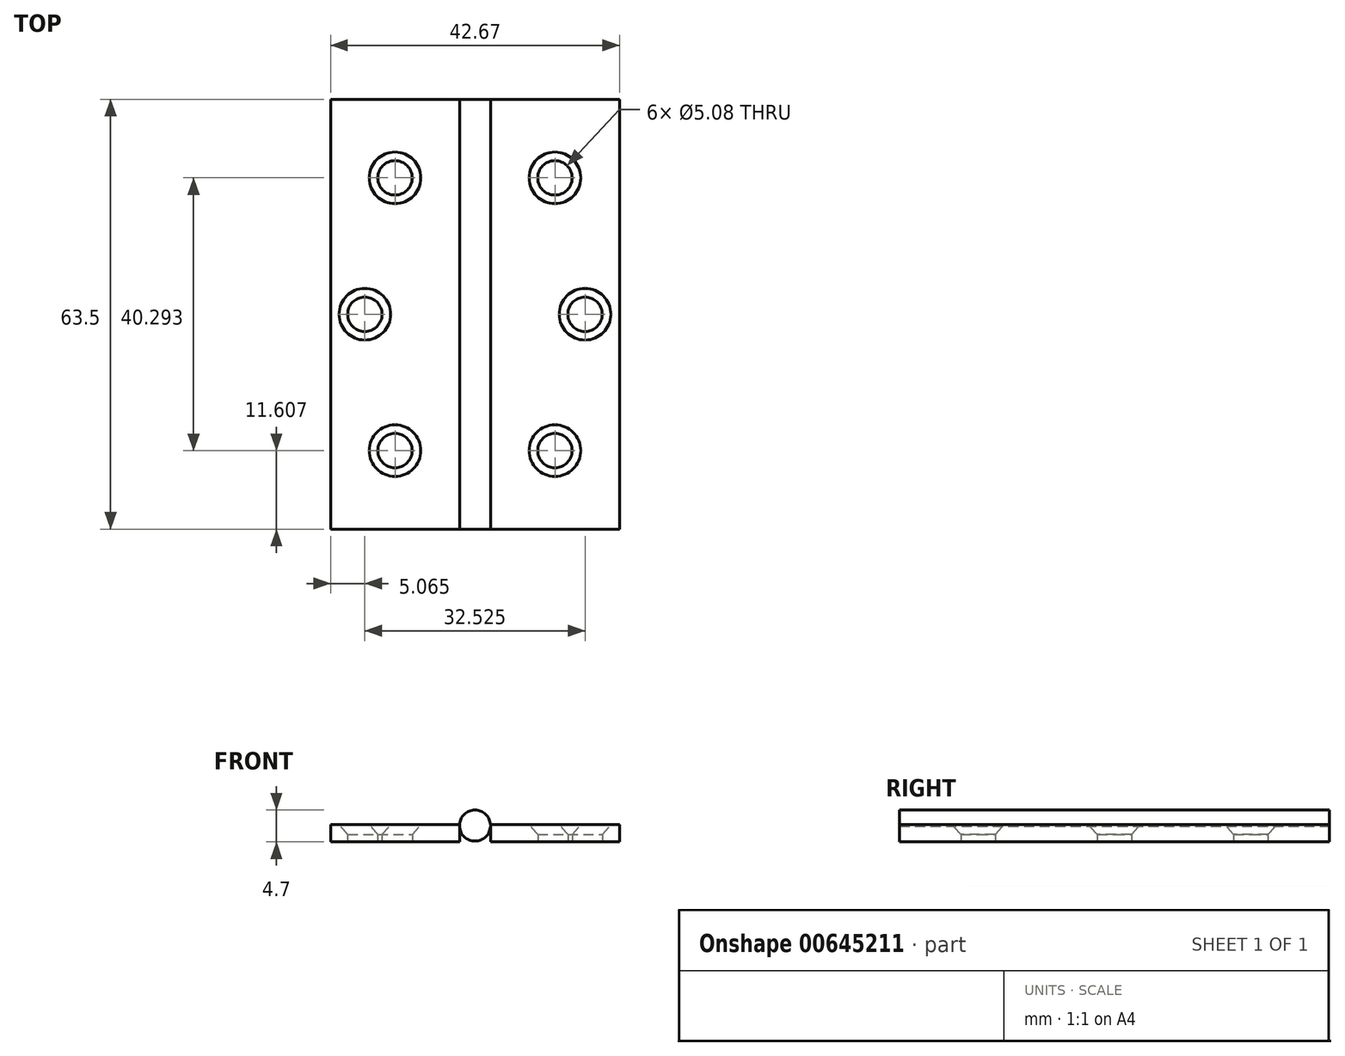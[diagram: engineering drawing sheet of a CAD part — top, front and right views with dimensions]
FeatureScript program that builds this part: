
annotation { "Feature Type Name" : "Feature", "Feature Type Description" : "" }
export const myFeature = defineFeature(function(context is Context, id is Id, definition is map)
    precondition{}
    {
        {
            var Q0;
            Q0=qCreatedBy(makeId("Top.planeOp"),FACE);
            var sketch = newSketch(context, id + "F0", { "sketchPlane" : qUnion([Q0])});
            skLineSegment(sketch, "E0.bottom", {"start": v(-55.16, 49.12) * mm, "end": v(-36.11, 49.12) * mm});
            skLineSegment(sketch, "E0.top", {"start": v(-55.16, -14.38) * mm, "end": v(-36.11, -14.38) * mm});
            skLineSegment(sketch, "E0.left", {"start": v(-55.16, 49.12) * mm, "end": v(-55.16, -14.38) * mm});
            skLineSegment(sketch, "E0.right", {"start": v(-36.11, 49.12) * mm, "end": v(-36.11, -14.38) * mm});
            skLineSegment(sketch, "E1.bottom", {"start": v(-31.54, -14.38) * mm, "end": v(-12.5, -14.38) * mm});
            skLineSegment(sketch, "E1.top", {"start": v(-31.54, 49.12) * mm, "end": v(-12.5, 49.12) * mm});
            skLineSegment(sketch, "E1.left", {"start": v(-31.54, -14.38) * mm, "end": v(-31.54, 49.12) * mm});
            skLineSegment(sketch, "E1.right", {"start": v(-12.5, -14.38) * mm, "end": v(-12.5, 49.12) * mm});
            skLineSegment(sketch, "E2", {"start": v(-45.64, 49.12) * mm, "end": v(-45.64, -14.38) * mm, "construction": true});
            skLineSegment(sketch, "E3", {"start": v(-22.02, -14.38) * mm, "end": v(-22.02, 49.12) * mm, "construction": true});
            skLineSegment(sketch, "E4", {"start": v(-12.5, 17.37) * mm, "end": v(-31.54, 17.37) * mm, "construction": true});
            skLineSegment(sketch, "E5", {"start": v(-36.11, 17.37) * mm, "end": v(-55.16, 17.37) * mm, "construction": true});
            skPoint(sketch, "E6", {"position": v(-22.02, -2.77) * mm});
            skPoint(sketch, "E7", {"position": v(-17.57, 17.37) * mm});
            skPoint(sketch, "E8", {"position": v(-22.02, 37.52) * mm});
            skPoint(sketch, "E9", {"position": v(-45.64, 37.52) * mm});
            skPoint(sketch, "E10", {"position": v(-50.1, 17.37) * mm});
            skPoint(sketch, "E11", {"position": v(-45.64, -2.77) * mm});
            skSolve(sketch);
        }
        {
            var Q0;
            Q0=makeQuery(id+"F0.imprint","IMPRINT",FACE,{"disambiguationData":[TD([[makeQuery(id+"F0.imprint","IMPRINT",EDGE,{"derivedFrom":sQuery(id+"F0.wireOp",EDGE,"E0.bottom")}),-1.0]])]});
            var Q1;
            Q1=makeQuery(id+"F0.imprint","IMPRINT",FACE,{"disambiguationData":[TD([[makeQuery(id+"F0.imprint","IMPRINT",EDGE,{"derivedFrom":sQuery(id+"F0.wireOp",EDGE,"E1.bottom")}),1.0]])]});
            extrude(context, id + "F1", {"entities" : qUnion([Q0, Q1]), "depth" : 2.54 * mm, "offsetDistance" : 25.4 * mm});
        }
        {
            var Q0;
            Q0=makeQuery(id+"F1.opExtrude","SWEPT_FACE",FACE,{"disambiguationData":[OSD([sQuery(id+"F0.wireOp",EDGE,"E0.bottom")])]});
            var sketch = newSketch(context, id + "F2", { "sketchPlane" : qUnion([Q0])});
            skLineSegment(sketch, "E12.0.0", {"start": v(12.5, 0) * mm, "end": v(31.54, 0) * mm});
            skLineSegment(sketch, "E12.0.1", {"start": v(31.54, 0) * mm, "end": v(31.54, 2.54) * mm});
            skLineSegment(sketch, "E12.0.2", {"start": v(31.54, 2.54) * mm, "end": v(12.5, 2.54) * mm});
            skLineSegment(sketch, "E12.0.3", {"start": v(12.5, 2.54) * mm, "end": v(12.5, 0) * mm});
            skCircle(sketch, "E13", {"center": v(33.83, 2.41) * mm, "radius": 2.29 * mm});
            skPoint(sketch, "E13.second.point", {"position": v(36.11, 2.54) * mm});
            skPoint(sketch, "E13.third.point", {"position": v(33.79, 4.7) * mm});
            skSolve(sketch);
        }
        {
            var Q0;
            {var subQ0=sQuery(id+"F2.wireOp",EDGE,"E13");var subQ1=sQuery(id+"F2.wireOp",EDGE,"E12.0.1");var subQ3=makeQuery(id+"F2.imprint","INTERSECT",VERTEX,{"derivedFrom":[subQ1,subQ0]});Q0=makeQuery(id+"F2.imprint","IMPRINT",FACE,{"disambiguationData":[TD([[makeQuery(id+"F2.imprint","IMPRINT",EDGE,{"disambiguationData":[TD([[subQ3,-1.0]])],"derivedFrom":subQ1}),-1.0]])]});}
            extrude(context, id + "F3", {"entities" : qUnion([Q0]), "oppositeDirection" : true, "depth" : 63.5 * mm, "offsetDistance" : 25.4 * mm});
        }
        {
            var Q0;
            Q0=makeQuery(id+"F1.opExtrude","CAP_FACE",FACE,{"disambiguationData":[OSD([sQuery(id+"F0.wireOp",EDGE,"E0.bottom"),sQuery(id+"F0.wireOp",EDGE,"E0.top"),sQuery(id+"F0.wireOp",EDGE,"E0.left"),sQuery(id+"F0.wireOp",EDGE,"E0.right")])],"isStart":false});
            var sketch = newSketch(context, id + "F4", { "sketchPlane" : qUnion([Q0])});
            skPoint(sketch, "E14.0", {"position": v(-50.1, 17.37) * mm});
            skPoint(sketch, "E14.1", {"position": v(-45.64, -2.77) * mm});
            skPoint(sketch, "E14.2", {"position": v(-22.02, -2.77) * mm});
            skPoint(sketch, "E14.3", {"position": v(-17.57, 17.37) * mm});
            skPoint(sketch, "E14.4", {"position": v(-22.02, 37.52) * mm});
            skPoint(sketch, "E14.5", {"position": v(-45.64, 37.52) * mm});
            skSolve(sketch);
        }
        {
            var Q0;
            Q0=sQuery(id+"F4.wireOp",VERTEX,"E14.1");
            var Q1;
            Q1=sQuery(id+"F4.wireOp",VERTEX,"E14.2");
            var Q2;
            Q2=sQuery(id+"F4.wireOp",VERTEX,"E14.3");
            var Q3;
            Q3=sQuery(id+"F4.wireOp",VERTEX,"E14.0");
            var Q4;
            Q4=sQuery(id+"F4.wireOp",VERTEX,"E14.5");
            var Q5;
            Q5=sQuery(id+"F4.wireOp",VERTEX,"E14.4");
            var Q6;
            Q6=makeQuery(id+"F1.opExtrude","SWEPT_BODY",BODY,{"disambiguationData":[OSD([sQuery(id+"F0.wireOp",EDGE,"E1.bottom"),sQuery(id+"F0.wireOp",EDGE,"E1.top"),sQuery(id+"F0.wireOp",EDGE,"E1.left"),sQuery(id+"F0.wireOp",EDGE,"E1.right")])]});
            var Q7;
            Q7=makeQuery(id+"F1.opExtrude","SWEPT_BODY",BODY,{"disambiguationData":[OSD([sQuery(id+"F0.wireOp",EDGE,"E0.bottom"),sQuery(id+"F0.wireOp",EDGE,"E0.top"),sQuery(id+"F0.wireOp",EDGE,"E0.left"),sQuery(id+"F0.wireOp",EDGE,"E0.right")])]});
            hole(context, id + "F5", {"style" : HoleStyle.C_SINK, "endStyle" : HoleEndStyle.THROUGH, "holeDiameter" : 5.08 * mm, "cSinkDiameter" : 7.62 * mm, "cSinkAngle" : 82 * degree, "majorDiameter" : 6.35 * mm, "isTappedThrough" : true, "tappedDepth" : 12.7 * mm, "tapClearance" : 3, "locations" : qUnion([Q0, Q1, Q2, Q3, Q4, Q5]), "scope" : qUnion([Q6, Q7]), "startStyle" : HoleStartStyle.SKETCH});
        }
    });
